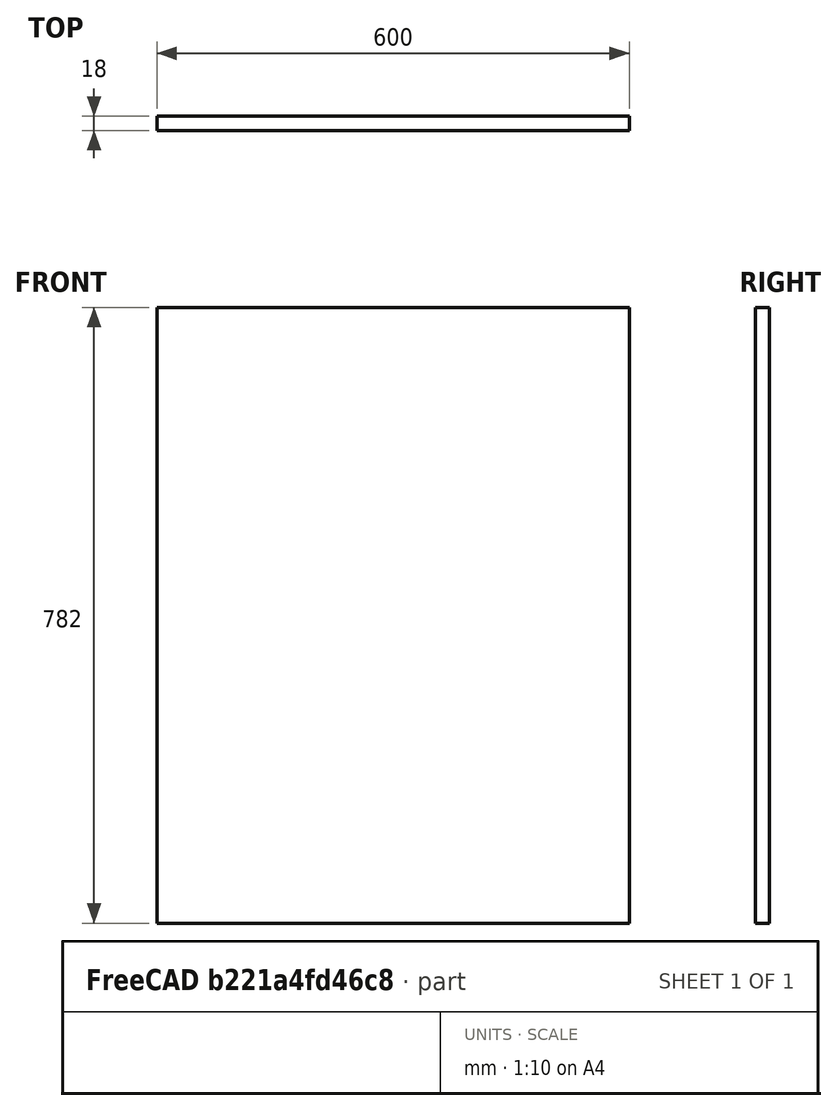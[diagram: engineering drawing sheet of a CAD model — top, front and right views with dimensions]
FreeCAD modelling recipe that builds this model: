
FCSTD DOCUMENT  (FreeCAD 0.18R4 (GitTag))
Label: side
License: All rights reserved
LicenseURL: http://en.wikipedia.org/wiki/All_rights_reserved
objects: Sketcher::SketchObject×1, PartDesign::Pad×1, PartDesign::Body×1
note: 4 computed .brp shape members not serialized (recipe doc carries the construction recipe); baked Part::Feature solids carry a one-line shape summary decoded from their .brp

FEATURE [Sketcher::SketchObject] Sketch
  MapMode = 5
  Placement = pos=(0,0,0) rot=(1,0,0;1.5708rad)
  Support = -> [XZ_Plane]
  sketch-geometry (4):
    g0: LineSegment StartX=0 StartY=0 StartZ=0 EndX=-600 EndY=0 EndZ=0
    g1: LineSegment StartX=-600 StartY=0 StartZ=0 EndX=-600 EndY=782 EndZ=0
    g2: LineSegment StartX=-600 StartY=782 StartZ=0 EndX=0 EndY=782 EndZ=0
    g3: LineSegment StartX=0 StartY=782 StartZ=0 EndX=0 EndY=0 EndZ=0
  constraints (11):
    c: Coincident(g0,g1)
    c: Coincident(g1,g2)
    c: Coincident(g2,g3)
    c: Coincident(g3,g0)
    c: Horizontal(g0)
    c: Horizontal(g2)
    c: Vertical(g1)
    c: Vertical(g3)
    c: Coincident(g0,g-1)
    c: DistanceX(g0,g0) = 600
    c: DistanceY(g3,g3) = 782
FEATURE [PartDesign::Pad] Pad
  Length = 18
  Length2 = 100
  Placement = pos=(0,0,0) rot=(1,0,0;1.5708rad)
  Profile = -> Sketch
  Type = 0
FEATURE [PartDesign::Body] Body
  Group = -> [Sketch,Pad]
  Origin = -> Origin
  Tip = -> Pad
